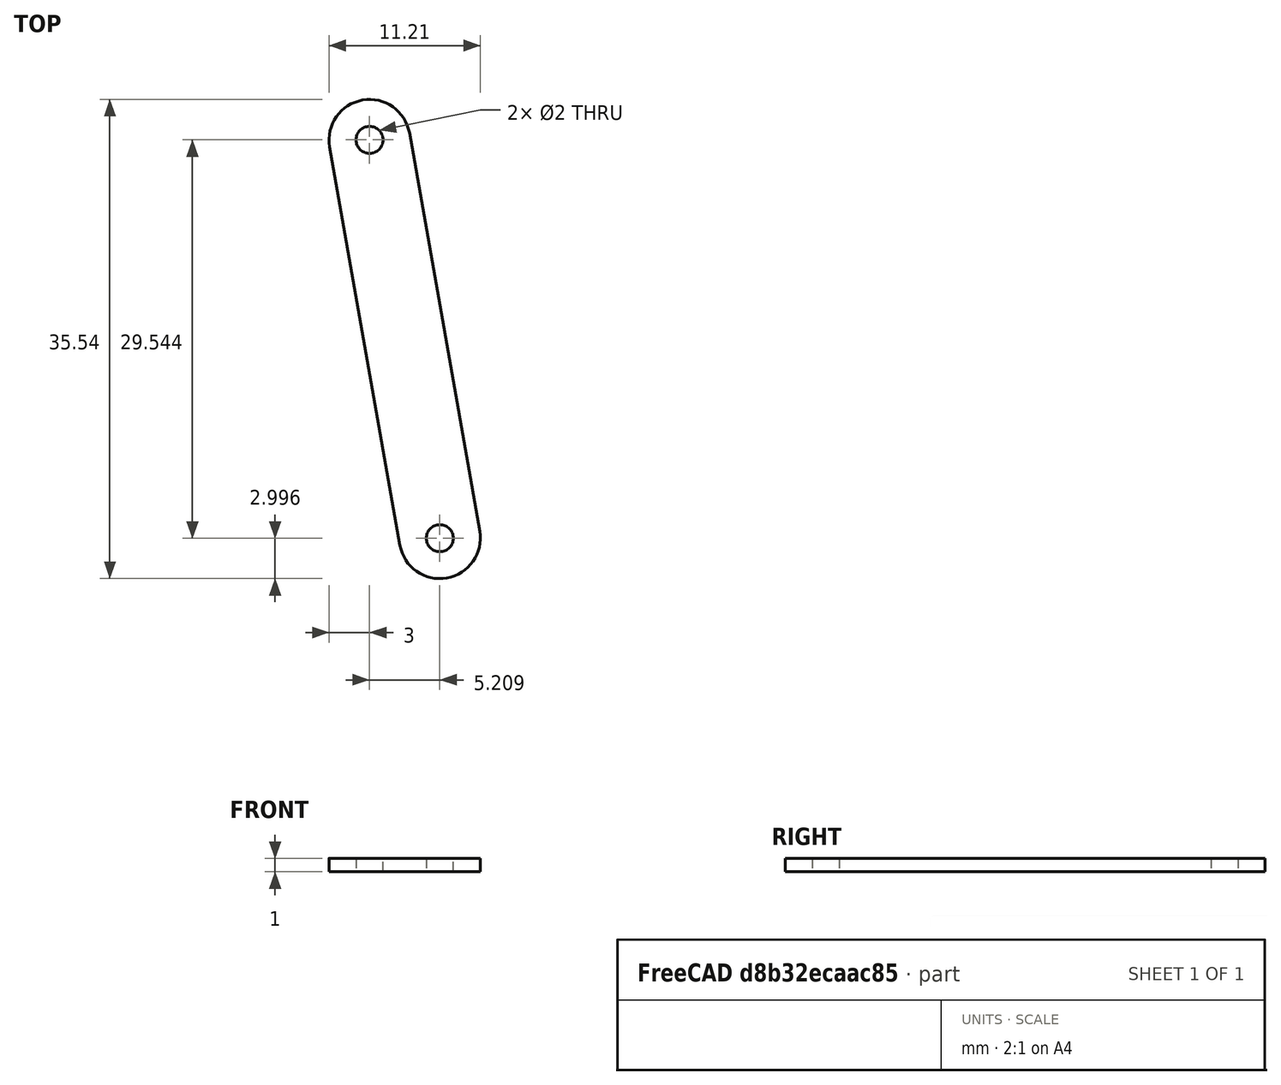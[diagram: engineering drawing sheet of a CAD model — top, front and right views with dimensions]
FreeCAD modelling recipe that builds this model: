
FCSTD DOCUMENT  (FreeCAD 0.19R24276 (Git))
Label: Left
License: All rights reserved
LicenseURL: http://en.wikipedia.org/wiki/All_rights_reserved
objects: Sketcher::SketchObject×1, PartDesign::Pad×1, PartDesign::Body×1
note: 4 computed .brp shape members not serialized (recipe doc carries the construction recipe); baked Part::Feature solids carry a one-line shape summary decoded from their .brp

FEATURE [Sketcher::SketchObject] Sketch
  FullyConstrained = true
  MapMode = 5
  Support = -> [XY_Plane]
  sketch-geometry (7):
    g0: ArcOfCircle CenterX=0 CenterY=0 CenterZ=0 NormalX=0 NormalY=0 NormalZ=1 AngleXU=0 Radius=3 StartAngle=0.174533 EndAngle=3.31613
    g1: ArcOfCircle CenterX=5.20945 CenterY=-29.5442 CenterZ=0 NormalX=0 NormalY=0 NormalZ=1 AngleXU=0 Radius=3 StartAngle=3.31613 EndAngle=6.45772
    g2: LineSegment StartX=-2.95442 StartY=-0.520945 StartZ=0 EndX=2.25502 EndY=-30.0652 EndZ=0
    g3: LineSegment StartX=2.95442 StartY=0.520945 StartZ=0 EndX=8.16387 EndY=-29.0233 EndZ=0
    g4: LineSegment StartX=0 StartY=0 StartZ=0 EndX=5.20945 EndY=-29.5442 EndZ=0
    g5: Circle CenterX=0 CenterY=0 CenterZ=0 NormalX=0 NormalY=0 NormalZ=1 AngleXU=0 Radius=1
    g6: Circle CenterX=5.20945 CenterY=-29.5442 CenterZ=0 NormalX=0 NormalY=0 NormalZ=1 AngleXU=0 Radius=1
  constraints (15):
    c: Tangent(g0,g3) = 1.5708
    c: Tangent(g0,g2) = -1.5708
    c: Tangent(g2,g1) = -1.5708
    c: Tangent(g3,g1) = 1.5708
    c: Equal(g0,g1)
    c: Coincident(g4,g0)
    c: Coincident(g4,g1)
    c: Distance(g4) = 30
    c: Radius(g0) = 3
    c: Coincident(g5,g4)
    c: Coincident(g6,g4)
    c: Diameter(g5) = 2
    c: Equal(g5,g6)
    c: Coincident(g4,g-1)
    c: Angle(g4,g-2) = 2.96706
FEATURE [PartDesign::Pad] Pad
  Direction = (1,1,1)
  Length = 1
  Length2 = 100
  Profile = -> Sketch
  Type = 0
FEATURE [PartDesign::Body] Body  label="Left"
  Group = -> [Sketch,Pad]
  Origin = -> Origin
  Tip = -> Pad
